# Revit family: Site-Waste_Management-EarthBin-EB505-bk7
name_source: partatom
category: Site
units: mm (PartAtom-declared; Revit-internal decimal feet)

## family parameters
Always vertical = Yes
Cut with Voids When Loaded = No
OmniClass Number = 23.70.30.21.14
OmniClass Title = Solid Waste Bins
Part Type = Normal
Round Connector Dimension = Use Diameter
Shared = No
Work Plane-Based = No

## types (1)
- Grey
    Assembly Code = E1090200
    CD_Depth = 5' - 10"
    CD_Depth In Ground = 5' - 2"
    CD_Feed Height = 3' - 9 1/4"
    CD_Finish Bin = Plastic-Polyethylene-EarthBin-Bin-Grey
    CD_Finish Feed Door = Plastic-Polyethylene-EarthBin-Feed_Door-Black
    CD_Finish Frame = Metal-Steel-EarthBin
    CD_Finish Lid = Plastic-Polyethylene-EarthBin-Lid-Grey
    CD_Height = 4' - 3 1/4"
    CD_Microsite = https://www.caddetails.com
    CD_Product Documentation Link = https://static1.squarespace.com
    CD_Product Name = Front Load Semi In-Ground EB500
    CD_Product Page URL = https://www.earthbin.com
    CD_Specification = https://static1.squarespace.com
    CD_Width = 6' - 8"
    Default Elevation = 0' - 0"
    Description = Rectangular waste & recycling
    Manufacturer = EarthBin
    Model = EB505
    Type Comments = 6.5 cu. yd. (5000 litres)
    URL = https://www.earthbin.com

## geometry (parser evidence)
native form markers: Sweep x12
no freeform markers — native parametric forms only
